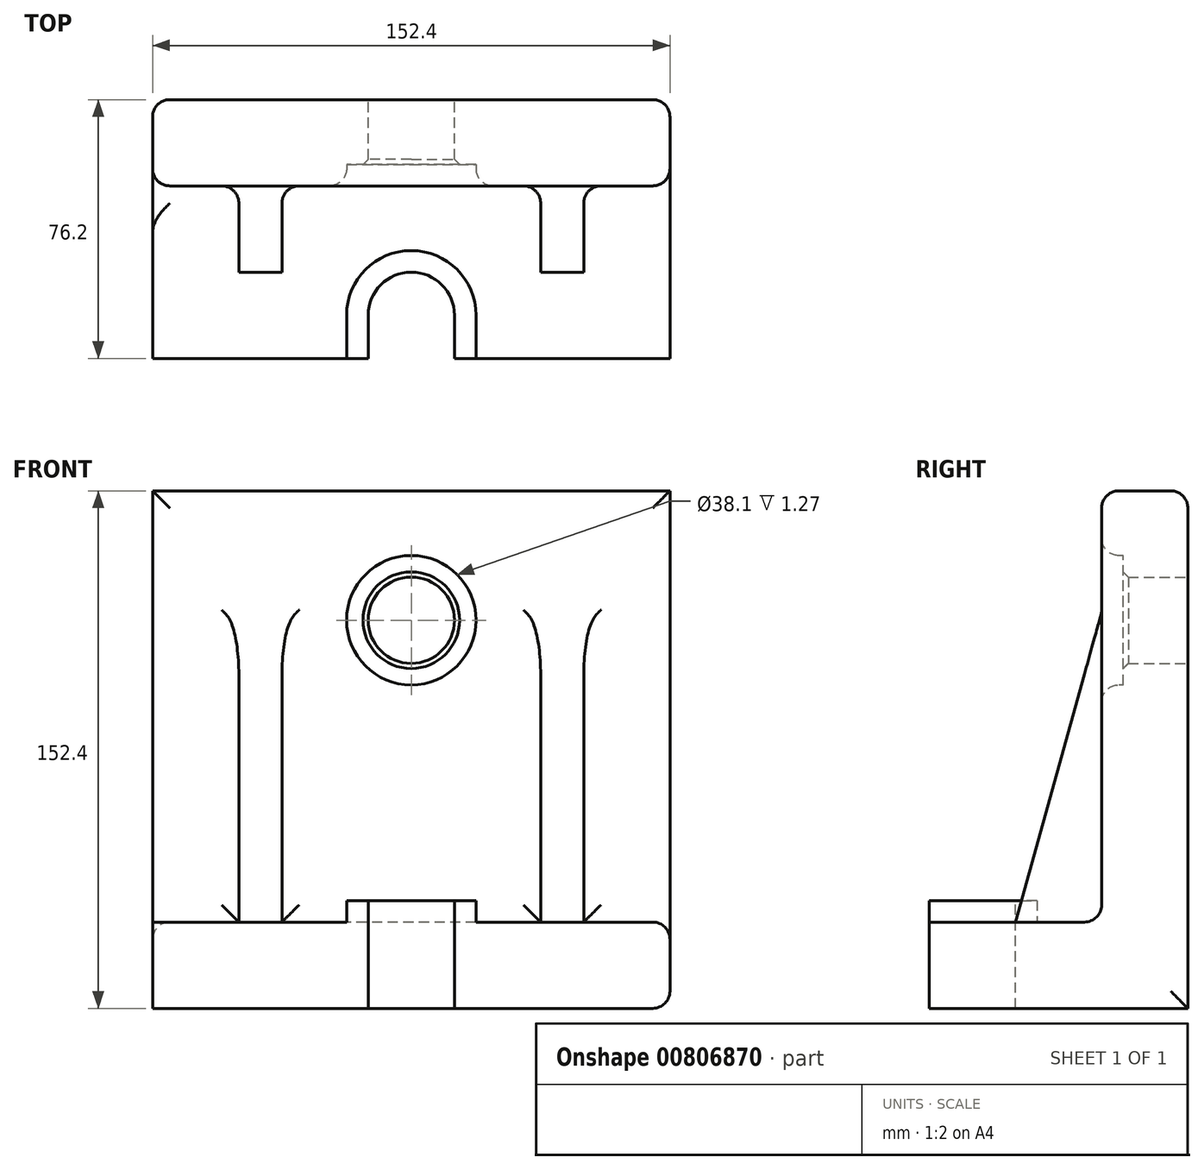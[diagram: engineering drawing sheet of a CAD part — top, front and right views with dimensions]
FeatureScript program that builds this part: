
annotation { "Feature Type Name" : "Feature", "Feature Type Description" : "" }
export const myFeature = defineFeature(function(context is Context, id is Id, definition is map)
    precondition{}
    {
        {
            var Q0;
            Q0=qCreatedBy(makeId("Right.planeOp"),FACE);
            var sketch = newSketch(context, id + "F0", { "sketchPlane" : qUnion([Q0])});
            skLineSegment(sketch, "E0", {"start": v(0, 152.4) * mm, "end": v(0, 0) * mm});
            skLineSegment(sketch, "E1", {"start": v(0, 0) * mm, "end": v(-76.2, 0) * mm});
            skLineSegment(sketch, "E2", {"start": v(-76.2, 0) * mm, "end": v(-76.2, 25.4) * mm});
            skLineSegment(sketch, "E3", {"start": v(-76.2, 25.4) * mm, "end": v(-25.4, 25.4) * mm});
            skLineSegment(sketch, "E4", {"start": v(-25.4, 25.4) * mm, "end": v(-25.4, 152.4) * mm});
            skLineSegment(sketch, "E5", {"start": v(-25.4, 152.4) * mm, "end": v(0, 152.4) * mm});
            skSolve(sketch);
        }
        {
            var Q0;
            Q0 = qSketchRegion(id + "F0", true);
            extrude(context, id + "F1", {"entities" : qUnion([Q0]), "endBound" : BoundingType.SYMMETRIC, "depth" : 152.4 * mm, "offsetDistance" : 25.4 * mm});
        }
        {
            var Q0;
            Q0=makeQuery(id+"F1.opExtrude","SWEPT_FACE",FACE,{"disambiguationData":[OSD([sQuery(id+"F0.wireOp",EDGE,"E0")])]});
            var sketch = newSketch(context, id + "F2", { "sketchPlane" : qUnion([Q0])});
            skCircle(sketch, "E6", {"center": v(0, 114.3) * mm, "radius": 12.7 * mm});
            skSolve(sketch);
        }
        {
            var Q0;
            Q0=makeQuery(id+"F2.imprint","IMPRINT",FACE,{"disambiguationData":[TD([[makeQuery(id+"F2.imprint","IMPRINT",EDGE,{"derivedFrom":sQuery(id+"F2.wireOp",EDGE,"E6")}),1.0]])]});
            extrude(context, id + "F3", {"entities" : qUnion([Q0]), "operationType" : NewBodyOperationType.REMOVE, "oppositeDirection" : true, "depth" : 41.66 * mm, "offsetDistance" : 25.4 * mm});
        }
        {
            var Q0;
            Q0=makeQuery(id+"F1.opExtrude","SWEPT_FACE",FACE,{"disambiguationData":[OSD([sQuery(id+"F0.wireOp",EDGE,"E3")])]});
            var sketch = newSketch(context, id + "F4", { "sketchPlane" : qUnion([Q0])});
            skLineSegment(sketch, "E7", {"start": v(-12.7, -76.2) * mm, "end": v(-12.7, -63.5) * mm});
            skLineSegment(sketch, "E8.MirrorCS", {"start": v(12.7, -76.2) * mm, "end": v(12.7, -63.5) * mm});
            skArc(sketch, "E9", {"start": v(12.7, -63.5) * mm, "mid": v(0, -50.8) * mm, "end": v(-12.7, -63.5) * mm});
            skSolve(sketch);
        }
        {
            var Q0;
            Q0 = qSketchRegion(id + "F4", true);
            var Q1;
            {var subQ0=sQuery(id+"F4.wireOp",EDGE,"E7");Q1=makeQuery(id+"F4.imprint","IMPRINT",FACE,{"disambiguationData":[TD([[makeQuery(id+"F4.imprint","IMPRINT",EDGE,{"derivedFrom":subQ0}),-1.0]])]});}
            extrude(context, id + "F5", {"entities" : qUnion([Q0, Q1]), "operationType" : NewBodyOperationType.REMOVE, "oppositeDirection" : true, "depth" : 25.4 * mm, "offsetDistance" : 25.4 * mm});
        }
        {
            var Q0;
            Q0=makeQuery(id+"F1.opExtrude","SWEPT_FACE",FACE,{"disambiguationData":[OSD([sQuery(id+"F0.wireOp",EDGE,"E4")])]});
            var sketch = newSketch(context, id + "F6", { "sketchPlane" : qUnion([Q0])});
            skLineSegment(sketch, "E10", {"start": v(0, 127) * mm, "end": v(0, 101.6) * mm, "construction": true});
            skCircle(sketch, "E11", {"center": v(0, 114.3) * mm, "radius": 19.05 * mm});
            skSolve(sketch);
        }
        {
            var Q0;
            Q0 = qSketchRegion(id + "F6", true);
            extrude(context, id + "F7", {"entities" : qUnion([Q0]), "operationType" : NewBodyOperationType.REMOVE, "oppositeDirection" : true, "depth" : 6.35 * mm, "offsetDistance" : 25.4 * mm});
        }
        {
            var Q0;
            Q0=makeQuery(id+"F1.opExtrude","SWEPT_FACE",FACE,{"disambiguationData":[OSD([sQuery(id+"F0.wireOp",EDGE,"E4")])]});
            var sketch = newSketch(context, id + "F8", { "sketchPlane" : qUnion([Q0])});
            skArc(sketch, "E12", {"start": v(76.2, 116.64) * mm, "mid": v(61.93, 142.72) * mm, "end": v(33.83, 152.4) * mm});
            skArc(sketch, "E13.MirrorCS", {"start": v(-76.2, 116.64) * mm, "mid": v(-61.93, 142.72) * mm, "end": v(-33.83, 152.4) * mm});
            skSolve(sketch);
        }
        {
            var Q0;
            Q0 = qSketchRegion(id + "F8", true);
            var Q1;
            {var subQ0=sQuery(id+"F8.wireOp",EDGE,"E12");var subQ1=sQuery(id+"F0.wireOp",EDGE,"E4");var subQ2=makeQuery(id+"F1.opExtrude","CAP_EDGE",EDGE,{"disambiguationData":[OSD([subQ1])],"isStart":false});var subQ3=makeQuery(id+"F8.imprint","INTERSECT",VERTEX,{"derivedFrom":[subQ2,subQ0]});Q1=makeQuery(id+"F8.imprint","IMPRINT",FACE,{"disambiguationData":[TD([[makeQuery(id+"F8.imprint","IMPRINT",EDGE,{"disambiguationData":[TD([[subQ3,-1.0]])],"derivedFrom":subQ0}),-1.0]])]});}
            var Q2;
            {var subQ0=sQuery(id+"F8.wireOp",EDGE,"E13.MirrorCS");var subQ1=sQuery(id+"F0.wireOp",EDGE,"E4");var subQ2=makeQuery(id+"F1.opExtrude","CAP_EDGE",EDGE,{"disambiguationData":[OSD([subQ1])],"isStart":true});var subQ3=makeQuery(id+"F8.imprint","INTERSECT",VERTEX,{"derivedFrom":[subQ2,subQ0]});Q2=makeQuery(id+"F8.imprint","IMPRINT",FACE,{"disambiguationData":[TD([[makeQuery(id+"F8.imprint","IMPRINT",EDGE,{"disambiguationData":[TD([[subQ3,-1.0]])],"derivedFrom":subQ0}),1.0]])]});}
            extrude(context, id + "F9", {"entities" : qUnion([Q0, Q1, Q2]), "operationType" : NewBodyOperationType.REMOVE, "oppositeDirection" : true, "depth" : 25.4 * mm, "offsetDistance" : 25.4 * mm});
        }
        {
            var Q0;
            Q0=qCreatedBy(makeId("Right.planeOp"),FACE);
            cPlane(context, id + "F10", {"entities" : qUnion([Q0]), "cplaneType" : CPlaneType.OFFSET, "offset" : 44.45 * mm, "width" : 152.4 * mm, "height" : 152.4 * mm});
        }
        {
            var Q0;
            Q0=qCreatedBy(id+"F10.planeOp",FACE);
            var sketch = newSketch(context, id + "F11", { "sketchPlane" : qUnion([Q0])});
            skLineSegment(sketch, "E14.0", {"start": v(-25.4, 25.4) * mm, "end": v(-25.4, 116.64) * mm});
            skLineSegment(sketch, "E15.0", {"start": v(-76.2, 25.4) * mm, "end": v(-25.4, 25.4) * mm});
            skLineSegment(sketch, "E16", {"start": v(-25.4, 116.64) * mm, "end": v(-50.8, 25.4) * mm});
            skSolve(sketch);
        }
        {
            var Q0;
            Q0 = qSketchRegion(id + "F11", true);
            extrude(context, id + "F12", {"entities" : qUnion([Q0]), "operationType" : NewBodyOperationType.ADD, "endBound" : BoundingType.SYMMETRIC, "depth" : 12.7 * mm, "offsetDistance" : 25.4 * mm});
        }
        {
            var Q0;
            Q0=makeQuery(id+"F1.opExtrude","SWEPT_BODY",BODY,{"disambiguationData":[OSD([sQuery(id+"F0.wireOp",EDGE,"E0"),sQuery(id+"F0.wireOp",EDGE,"E1"),sQuery(id+"F0.wireOp",EDGE,"E2"),sQuery(id+"F0.wireOp",EDGE,"E3"),sQuery(id+"F0.wireOp",EDGE,"E4"),sQuery(id+"F0.wireOp",EDGE,"E5")])]});
            var Q1;
            Q1=qCreatedBy(makeId("Right.planeOp"),FACE);
            mirror(context, id + "F13", {"operationType" : NewBodyOperationType.ADD, "entities" : qUnion([Q0]), "mirrorPlane" : qUnion([Q1])});
        }
        {
            var Q0;
            Q0=makeQuery(id+"F7.boolean.opBoolean","INTERSECT",EDGE,{"derivedFrom":[makeQuery(id+"F3.boolean.opBoolean","COPY",FACE,{"derivedFrom":makeQuery(id+"F3.opExtrude","SWEPT_FACE",FACE,{"disambiguationData":[OSD([sQuery(id+"F2.wireOp",EDGE,"E6")])]})}),makeQuery(id+"F7.opExtrude","CAP_FACE",FACE,{"disambiguationData":[OSD([sQuery(id+"F6.wireOp",EDGE,"E11")])],"isStart":false})]});
            var Q1;
            Q1=makeQuery(id+"F7.boolean.opBoolean","COPY",EDGE,{"derivedFrom":makeQuery(id+"F7.opExtrude","CAP_EDGE",EDGE,{"disambiguationData":[OSD([sQuery(id+"F6.wireOp",EDGE,"E11")])],"isStart":true})});
            chamfer(context, id + "F14", {"entities" : qUnion([Q0, Q1]), "width" : 1.52 * mm, "tangentPropagation" : true});
        }
        {
            var Q0;
            Q0=makeQuery(id+"F1.opExtrude","SWEPT_FACE",FACE,{"disambiguationData":[OSD([sQuery(id+"F0.wireOp",EDGE,"E3")])]});
            var sketch = newSketch(context, id + "F15", { "sketchPlane" : qUnion([Q0])});
            skLineSegment(sketch, "E17.0", {"start": v(19.05, -76.2) * mm, "end": v(19.05, -63.5) * mm});
            skArc(sketch, "E17.1", {"start": v(19.05, -63.5) * mm, "mid": v(0, -44.45) * mm, "end": v(-19.05, -63.5) * mm});
            skLineSegment(sketch, "E17.2", {"start": v(-19.05, -76.2) * mm, "end": v(-19.05, -63.5) * mm});
            skLineSegment(sketch, "E18", {"start": v(-19.05, -76.2) * mm, "end": v(-12.7, -76.2) * mm});
            skLineSegment(sketch, "E19", {"start": v(12.7, -76.2) * mm, "end": v(19.05, -76.2) * mm});
            skLineSegment(sketch, "E20", {"start": v(12.7, -76.2) * mm, "end": v(12.7, -63.5) * mm});
            skLineSegment(sketch, "E21", {"start": v(12.7, -63.5) * mm, "end": v(12.7, -76.2) * mm});
            skLineSegment(sketch, "E22", {"start": v(-12.7, -76.2) * mm, "end": v(-12.7, -63.5) * mm});
            skLineSegment(sketch, "E23", {"start": v(-12.7, -63.5) * mm, "end": v(-12.7, -76.2) * mm});
            skArc(sketch, "E24", {"start": v(12.7, -63.5) * mm, "mid": v(0, -50.8) * mm, "end": v(-12.7, -63.5) * mm});
            skSolve(sketch);
        }
        {
            var Q0;
            Q0 = qSketchRegion(id + "F15", true);
            extrude(context, id + "F16", {"entities" : qUnion([Q0]), "operationType" : NewBodyOperationType.ADD, "depth" : 6.35 * mm, "offsetDistance" : 25.4 * mm});
        }
        {
            var Q0;
            Q0=makeQuery(id+"F13.opPattern","COPY",EDGE,{"derivedFrom":makeQuery(id+"F12.opExtrude","CAP_EDGE",EDGE,{"disambiguationData":[OSD([sQuery(id+"F11.wireOp",EDGE,"E15.0")])],"isStart":true}),"instanceName":"1"});
            var Q1;
            Q1=makeQuery(id+"F13.opPattern","COPY",EDGE,{"derivedFrom":makeQuery(id+"F12.opExtrude","CAP_EDGE",EDGE,{"disambiguationData":[OSD([sQuery(id+"F11.wireOp",EDGE,"E14.0")])],"isStart":true}),"instanceName":"1"});
            var Q2;
            Q2=makeQuery(id+"F13.opPattern","COPY",EDGE,{"derivedFrom":makeQuery(id+"F12.opExtrude","SWEPT_EDGE",EDGE,{"disambiguationData":[OSD([sQuery(id+"F11.wireOp",EDGE,"E15.0"),sQuery(id+"F11.wireOp",EDGE,"E16")])]}),"instanceName":"1"});
            var Q3;
            Q3=makeQuery(id+"F13.opPattern","COPY",EDGE,{"derivedFrom":makeQuery(id+"F12.opExtrude","CAP_EDGE",EDGE,{"disambiguationData":[OSD([sQuery(id+"F11.wireOp",EDGE,"E15.0")])],"isStart":false}),"instanceName":"1"});
            var Q4;
            {var subQ0=sQuery(id+"F0.wireOp",EDGE,"E4");var subQ1=sQuery(id+"F0.wireOp",EDGE,"E3");var subQ5=sQuery(id+"F11.wireOp",EDGE,"E16");var subQ6=sQuery(id+"F11.wireOp",EDGE,"E15.0");var subQ7=sQuery(id+"F11.wireOp",EDGE,"E14.0");Q4=makeQuery(id+"F13.boolean.opBoolean","SPLIT",EDGE,{"disambiguationData":[TD([makeQuery(id+"F13.opPattern","COPY",FACE,{"derivedFrom":makeQuery(id+"F12.opExtrude","CAP_FACE",FACE,{"disambiguationData":[OSD([subQ7,subQ6,subQ5])],"isStart":false}),"instanceName":"1"})])],"derivedFrom":makeQuery(id+"F12.boolean.opBoolean","SPLIT",EDGE,{"disambiguationData":[TD([makeQuery(id+"F12.opExtrude","CAP_FACE",FACE,{"disambiguationData":[OSD([subQ7,subQ6,subQ5])],"isStart":true})])],"derivedFrom":makeQuery(id+"F1.opExtrude","SWEPT_EDGE",EDGE,{"disambiguationData":[OSD([subQ1,subQ0])]})})});}
            var Q5;
            Q5=makeQuery(id+"F16.opExtrude","CAP_EDGE",EDGE,{"disambiguationData":[OSD([sQuery(id+"F15.wireOp",EDGE,"E17.0")])],"isStart":true});
            var Q6;
            Q6=makeQuery(id+"F1.opExtrude","CAP_EDGE",EDGE,{"disambiguationData":[OSD([sQuery(id+"F0.wireOp",EDGE,"E3")])],"isStart":false});
            var Q7;
            Q7=makeQuery(id+"F1.opExtrude","CAP_EDGE",EDGE,{"disambiguationData":[OSD([sQuery(id+"F0.wireOp",EDGE,"E4")])],"isStart":false});
            var Q8;
            Q8=makeQuery(id+"F9.boolean.opBoolean","COPY",EDGE,{"derivedFrom":makeQuery(id+"F9.opExtrude","CAP_EDGE",EDGE,{"disambiguationData":[OSD([sQuery(id+"F8.wireOp",EDGE,"E12")])],"isStart":true})});
            var Q9;
            Q9=makeQuery(id+"F1.opExtrude","CAP_EDGE",EDGE,{"disambiguationData":[OSD([sQuery(id+"F0.wireOp",EDGE,"E1")])],"isStart":false});
            var Q10;
            Q10=makeQuery(id+"F1.opExtrude","CAP_EDGE",EDGE,{"disambiguationData":[OSD([sQuery(id+"F0.wireOp",EDGE,"E0")])],"isStart":false});
            var Q11;
            Q11=makeQuery(id+"F9.boolean.opBoolean","COPY",EDGE,{"derivedFrom":makeQuery(id+"F9.opExtrude","CAP_EDGE",EDGE,{"disambiguationData":[OSD([sQuery(id+"F8.wireOp",EDGE,"E12")])],"isStart":false})});
            var Q12;
            Q12=makeQuery(id+"F1.opExtrude","SWEPT_EDGE",EDGE,{"disambiguationData":[OSD([sQuery(id+"F0.wireOp",EDGE,"E0"),sQuery(id+"F0.wireOp",EDGE,"E5")])]});
            var Q13;
            Q13=makeQuery(id+"F1.opExtrude","CAP_EDGE",EDGE,{"disambiguationData":[OSD([sQuery(id+"F0.wireOp",EDGE,"E0")])],"isStart":true});
            var Q14;
            Q14=makeQuery(id+"F9.boolean.opBoolean","COPY",EDGE,{"derivedFrom":makeQuery(id+"F9.opExtrude","CAP_EDGE",EDGE,{"disambiguationData":[OSD([sQuery(id+"F8.wireOp",EDGE,"E13.MirrorCS")])],"isStart":false})});
            var Q15;
            Q15=makeQuery(id+"F1.opExtrude","SWEPT_FACE",FACE,{"disambiguationData":[OSD([sQuery(id+"F0.wireOp",EDGE,"E4")])]});
            fillet(context, id + "F17", {"entities" : qUnion([Q0, Q1, Q2, Q3, Q4, Q5, Q6, Q7, Q8, Q9, Q10, Q11, Q12, Q13, Q14, Q15]), "radius" : 5.08 * mm, "tangentPropagation" : true, "allowEdgeOverflow" : false});
        }
    });
